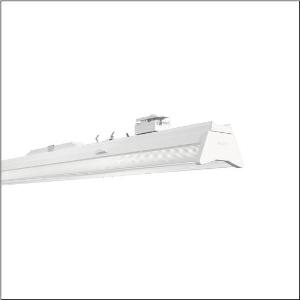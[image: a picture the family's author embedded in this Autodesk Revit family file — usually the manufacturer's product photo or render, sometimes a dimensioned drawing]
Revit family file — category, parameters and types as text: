
# Revit family: licross_r__11_performance_mo_51td16cn49xg_61c3
name_source: partatom
category: Lighting Fixtures
units: mm (PartAtom-declared; Revit-internal decimal feet)

## family parameters
Cut with Voids When Loaded = No
Host = Face
Light Source = No
Part Type = Normal
Room Calculation Point = No
Round Connector Dimension = Use Diameter
Shared = No

## types (1)
- --- (1 x LED, 9190 lm, 49.4 W, 4000K)
    Apparent Load = 49 VA
    CIE Flux Codes = 66 88 96 79 100
    Color Rendering = 80
    Color Temperature = 4000K
    Default Elevation = 1800 mm
    Description = Licross® 11 Performance MO, luminaire insert, of sheet steel, galvanised, coil coated, white, length: 1.500mm, width: 120mm, height: 123mm, LED rated luminous flux: 9.190lm, light colour: 840, control gear: ON/OFF Multilumen, CLOi, with plug, 3-pole, with phase selection, mains connection: 220..240V, AC, 50/60Hz, start of lifetime: 49W, end of service life: 55W, halogen-free wiring, primary light control with lens, of plastic, primary optical cover: cover, of PMMA, light emission: direct/indirect distribution, primary light characteristic: symmetric, protection rating (complete): IP54, insulation class (complete): insulation class I (protective earthing), certification: CE, ENEC, VDE, UKCA, protection symbol: D if used in an environment with non-conductive dust loads with corresponding accessories, impact resistance: IK06, permissible ambient temperature for indoor applications: -35..+40°C, corresponds to IFS (International Featured Standards) requirements for safety and quality in the food industry, reducing of maximum allowable ambient temperature of 5°C with ceiling mounting, LABS conformity tested according to VDMA 24364:2018-05, packaging unit: 1 piece
    Height = 114 mm
    Lamp = 1 x LED
    Lamp Light Flux = 9190 lm
    Lamp Power = 49.4 W
    Lamp count = 1
    Length = 1500 mm
    Luminous efficacy = 186 lm/W
    Manufacturer = Siteco
    ModVariant = No
    Model = 51TD16CN49XG
    Mounting Place = Ceiling
    Mounting Type = Pendant
    Number of Poles = 1
    OnlyDefault = Yes
    Power Factor = 1
    Product Name = Licross® 11 Performance MO
    Product group = luminaire insert
    ProductGroupID = 901
    Protection Class = Protection class I
    Protection Degree = IP 54
    RLX_Detail_Level = 1
    RLX_Emergency_Light_Flux = 0 lm
    RLX_Emergency_Type = 0
    RLX_Emergency_Type_DB = No
    RlxData = <blob elided: 31845 chars, md5=48397a57>
    Socket = socket
    Standby Power = 0 W
    System Light Flux = 9190 lm
    System Power = 49 W
    Type Comments = factory setting: luminous flux: 100 % | (A | C | E) | 113 mA
    Type Image = l_1256138.jpg
    URL = http://relux.com
    VarID = @adj_055433
    Voltage = 0 V
    Weight = 0.00 kg
    Width = 120 mm

## geometry (parser evidence)
native form markers: Blend x4, Sweep x13
no freeform markers — native parametric forms only
